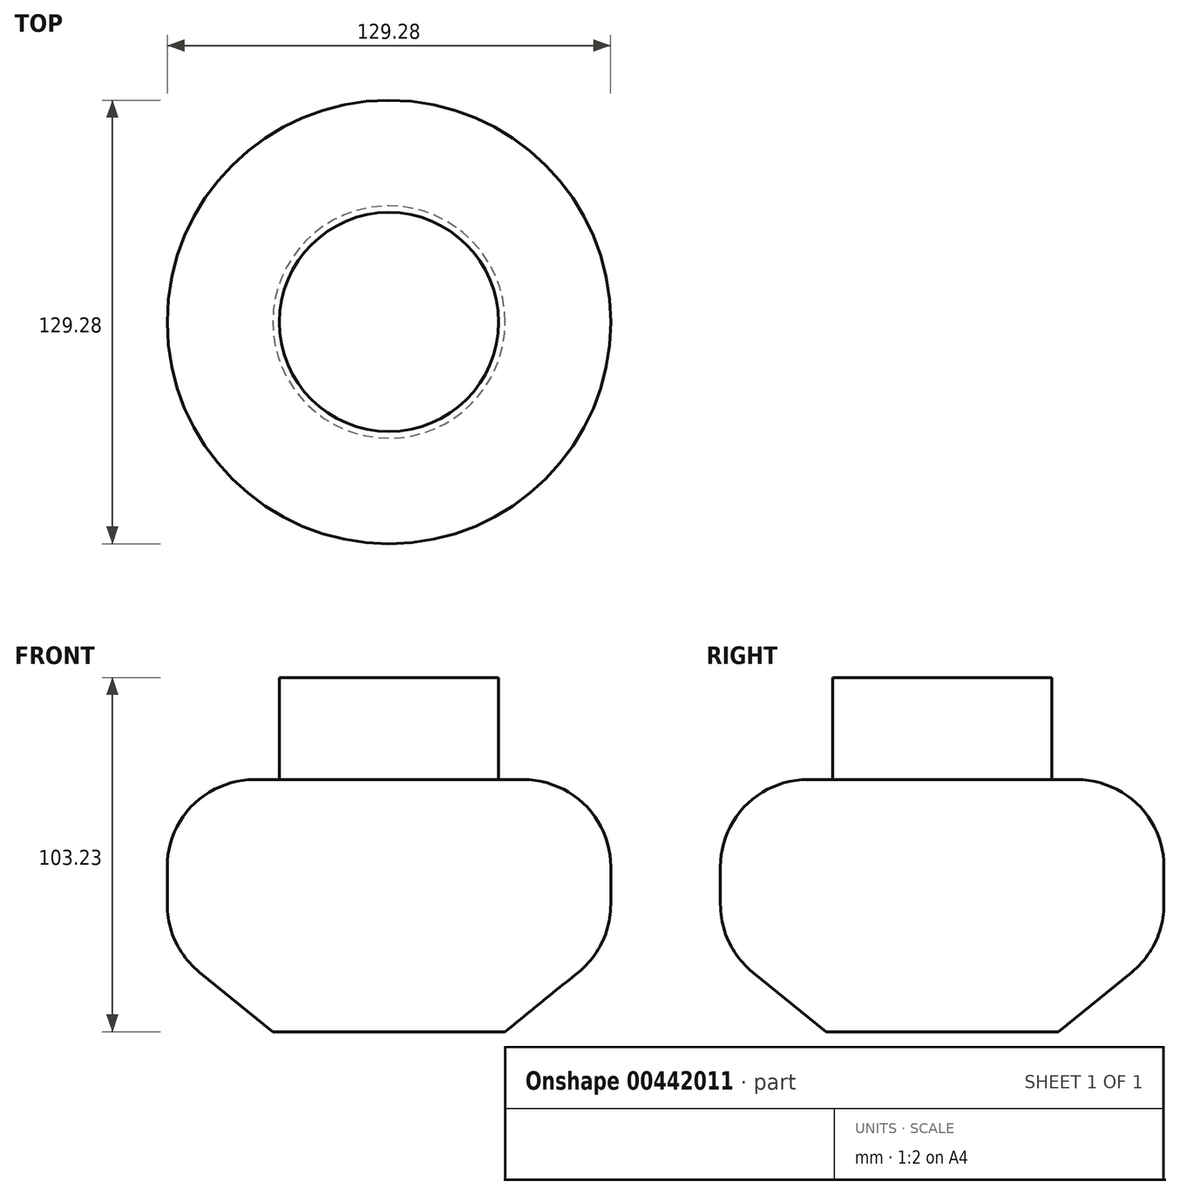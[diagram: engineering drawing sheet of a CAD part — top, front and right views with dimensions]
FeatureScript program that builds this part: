
annotation { "Feature Type Name" : "Feature", "Feature Type Description" : "" }
export const myFeature = defineFeature(function(context is Context, id is Id, definition is map)
    precondition{}
    {
        {
            var Q0;
            Q0=qCreatedBy(makeId("Front.planeOp"),FACE);
            var sketch = newSketch(context, id + "F0", { "sketchPlane" : qUnion([Q0])});
            skLineSegment(sketch, "E0", {"start": v(0, 0) * mm, "end": v(-33.85, 0) * mm});
            skLineSegment(sketch, "E1", {"start": v(-33.85, 0) * mm, "end": v(-55.26, 17.39) * mm});
            skLineSegment(sketch, "E2", {"start": v(-64.64, 37.1) * mm, "end": v(-64.64, 73.49) * mm});
            skLineSegment(sketch, "E3", {"start": v(-64.64, 73.49) * mm, "end": v(-31.94, 73.49) * mm});
            skLineSegment(sketch, "E4", {"start": v(-31.94, 73.49) * mm, "end": v(-31.94, 103.23) * mm});
            skLineSegment(sketch, "E5", {"start": v(-31.94, 103.23) * mm, "end": v(0, 103.23) * mm});
            skLineSegment(sketch, "E6", {"start": v(0, 103.23) * mm, "end": v(0, 0) * mm});
            skPoint(sketch, "E7.visualSharp", {"position": v(-64.64, 25.01) * mm});
            skArc(sketch, "E7.filletArc", {"start": v(-64.64, 37.1) * mm, "mid": v(-62.18, 26.19) * mm, "end": v(-55.26, 17.39) * mm});
            skSolve(sketch);
        }
        {
            var Q0;
            Q0=makeQuery(id+"F0.imprint","IMPRINT",FACE,{"disambiguationData":[TD([[makeQuery(id+"F0.imprint","IMPRINT",EDGE,{"derivedFrom":sQuery(id+"F0.wireOp",EDGE,"E0")}),-1.0]])]});
            var Q1;
            Q1=sQuery(id+"F0.wireOp",EDGE,"E6");
            revolve(context, id + "F1", {"entities" : qUnion([Q0]), "axis" : qUnion([Q1]), "revolveType" : RevolveType.FULL});
        }
        {
            var Q0;
            Q0=makeQuery(id+"F1.opRevolve","SWEPT_EDGE",EDGE,{"disambiguationData":[OSD([sQuery(id+"F0.wireOp",EDGE,"E2"),sQuery(id+"F0.wireOp",EDGE,"E3")])]});
            fillet(context, id + "F2", {"entities" : qUnion([Q0]), "radius" : 25.4 * mm, "tangentPropagation" : true, "allowEdgeOverflow" : false});
        }
    });
